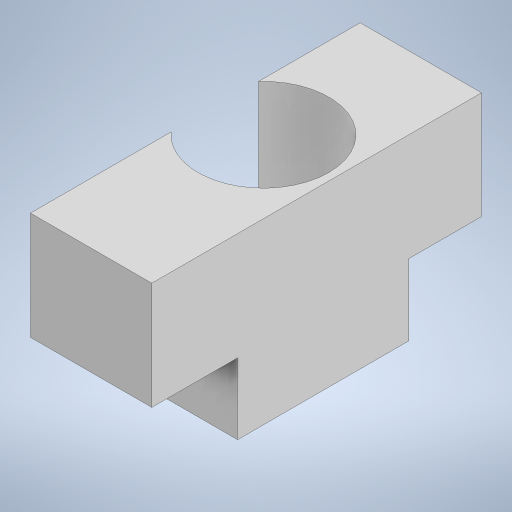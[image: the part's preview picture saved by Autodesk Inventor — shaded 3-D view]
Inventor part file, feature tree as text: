
AUTODESK INVENTOR PART (.ipt)
format: ipt  version: 2024.2 (Build 282272000, 272)  size: 324,096 bytes
history: native  units: in
note: dims shown in document units (in); Inventor stores cm internally (conversion verified against a paired STEP export)
features: extrude x11, sketch x11, projected_geometry x3
ambient origin geometry x8: Origin, YZ Plane, XZ Plane, XY Plane, X Axis, Y Axis, Z Axis, Center Point
bodies: Solid1 (feature_tree)
feature tree (25):
  extrude  "Extrusion1"  Depth=4.0in
  extrude  "Extrusion2"  Depth=0.1875in TaperAngle=0.0deg
  extrude  "Extrusion3"  TaperAngle=0.0deg  [1 undecoded]
  extrude  "Extrusion4"  Depth=1.0in
  extrude  "Extrusion5"  Depth=0.1875in
  extrude  "Extrusion6"  Depth=0.1875in
  extrude  "Extrusion7"  Depth=0.3937in TaperAngle=0.0deg
  extrude  "Extrusion8"  TaperAngle=0.0deg  [1 undecoded]
  extrude  "Extrusion9"  Depth=1.0in TaperAngle=0.0deg
  extrude  "Extrusion10"  Depth=0.6in TaperAngle=0.0deg
  extrude  "Extrusion11"  Depth=0.59in TaperAngle=0.0deg
  sketch  "Sketch1"  dims[d0=4.0in d1=4.0in]
  sketch  "Sketch2"  dims[d2=0.43in d3=0.1875in d4=0.0in]
  sketch  "Sketch3"  dims[d5=1.0in d6=0.0in]
  sketch  "Sketch4"  dims[d7=0.0in d8=0.0in d9=1.0in]
  sketch  "Sketch5"  dims[d10=0.16in d11=0.1875in]
  sketch  "Sketch6"  dims[d12=0.3149in d14=0.1875in]
  projected_geometry  "Projected Loop1"
  sketch  "Sketch7"  dims[d15=1.5748in d17=0.3936in d18=0.3937in d20=1.0in d22=1.0in d23=0.0in]
  sketch  "Sketch10"  dims[d24=0.075in d25=0.0in]
  sketch  "Sketch11"  dims[d26=0.311in d27=1.0in d28=0.0in]
  sketch  "Sketch12"  dims[d29=0.0in d30=0.0in d31=0.6in d32=0.0in]
  projected_geometry  "Projected Loop2"
  sketch  "Sketch13"  dims[d33=0.9in d34=0.59in d35=0.0in d36=0.5in d37=0.59in d38=0.0in d39=0.2in d40=0.59in d41=0.0in d42=0.1in d43=0.0in d44=0.54in d45=0.0in d13=0.0344in]
  projected_geometry  "Projected Loop3"
note: 2 required parameter values undecoded (feature->parameter linkage not recoverable at this tier; creation-order binding heuristic only, values carry confidence <= 0.55)
